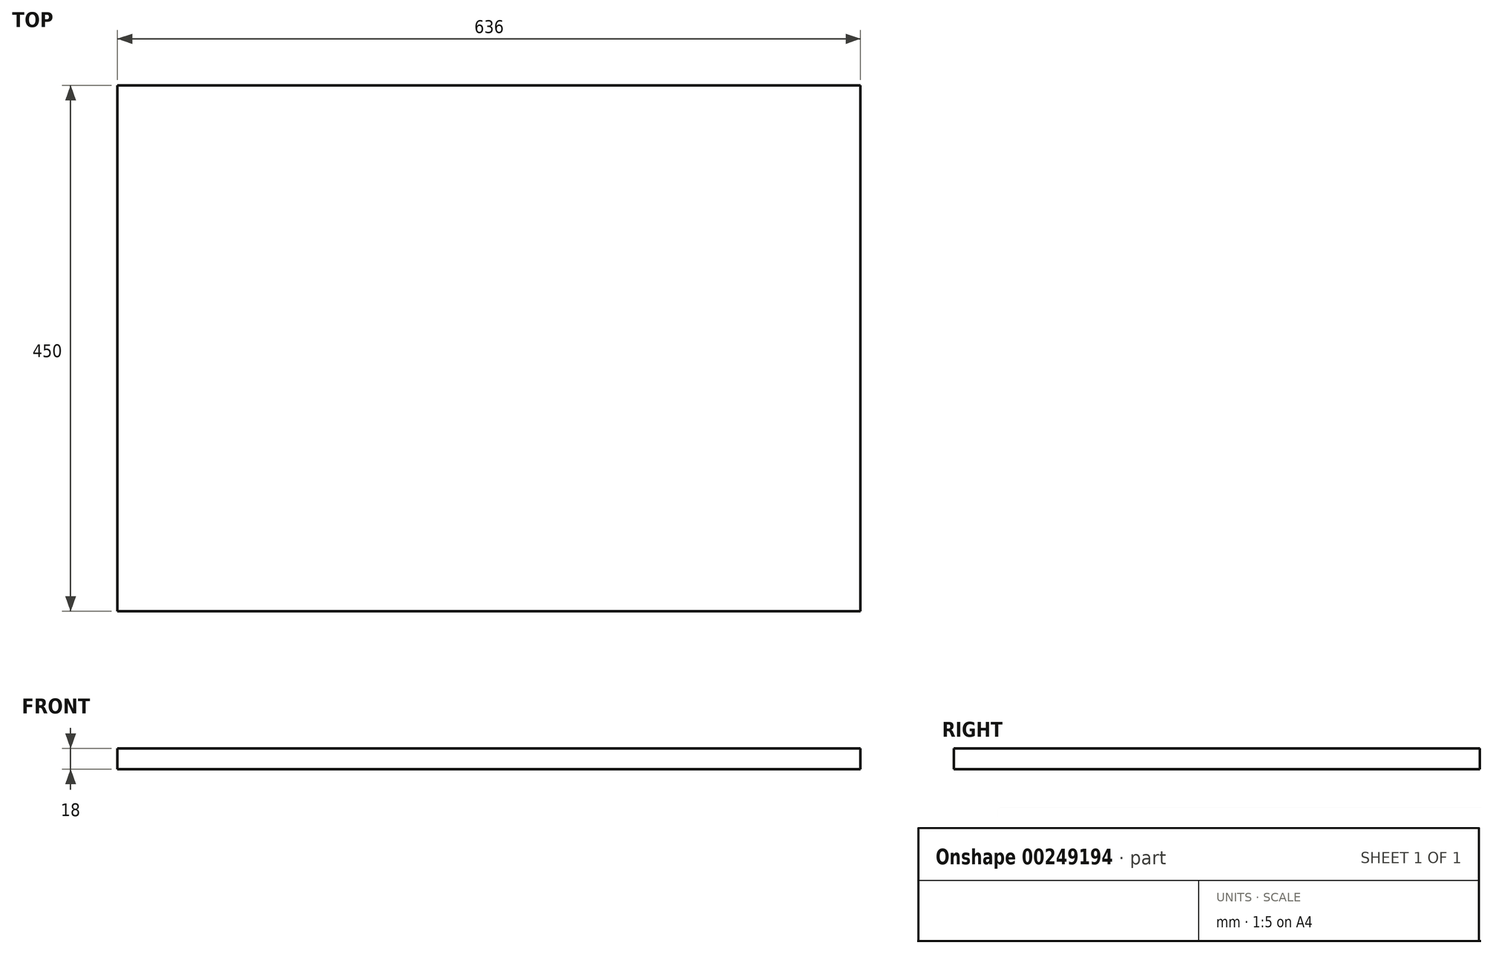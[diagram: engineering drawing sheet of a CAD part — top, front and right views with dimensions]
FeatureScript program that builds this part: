
annotation { "Feature Type Name" : "Feature", "Feature Type Description" : "" }
export const myFeature = defineFeature(function(context is Context, id is Id, definition is map)
    precondition{}
    {
        {
            var Q0;
            Q0=qCreatedBy(makeId("Top.planeOp"),FACE);
            var sketch = newSketch(context, id + "F0", { "sketchPlane" : qUnion([Q0])});
            skLineSegment(sketch, "E0.bottom", {"start": v(318, 225) * mm, "end": v(-318, 225) * mm});
            skLineSegment(sketch, "E0.top", {"start": v(318, -225) * mm, "end": v(-318, -225) * mm});
            skLineSegment(sketch, "E0.right", {"start": v(-318, 225) * mm, "end": v(-318, -225) * mm});
            skPoint(sketch, "E0.middle", {"position": v(0, 0) * mm});
            skPoint(sketch, "E1.middle", {"position": v(318, 225) * mm});
            skLineSegment(sketch, "E2", {"start": v(318, 225) * mm, "end": v(318, -225) * mm});
            skSolve(sketch);
        }
        {
            var Q0;
            Q0=makeQuery(id+"F0.imprint","IMPRINT",FACE,{"disambiguationData":[TD([[makeQuery(id+"F0.imprint","IMPRINT",EDGE,{"derivedFrom":sQuery(id+"F0.wireOp",EDGE,"E0.bottom")}),1.0]])]});
            extrude(context, id + "F1", {"entities" : qUnion([Q0]), "depth" : 18 * mm});
        }
    });
